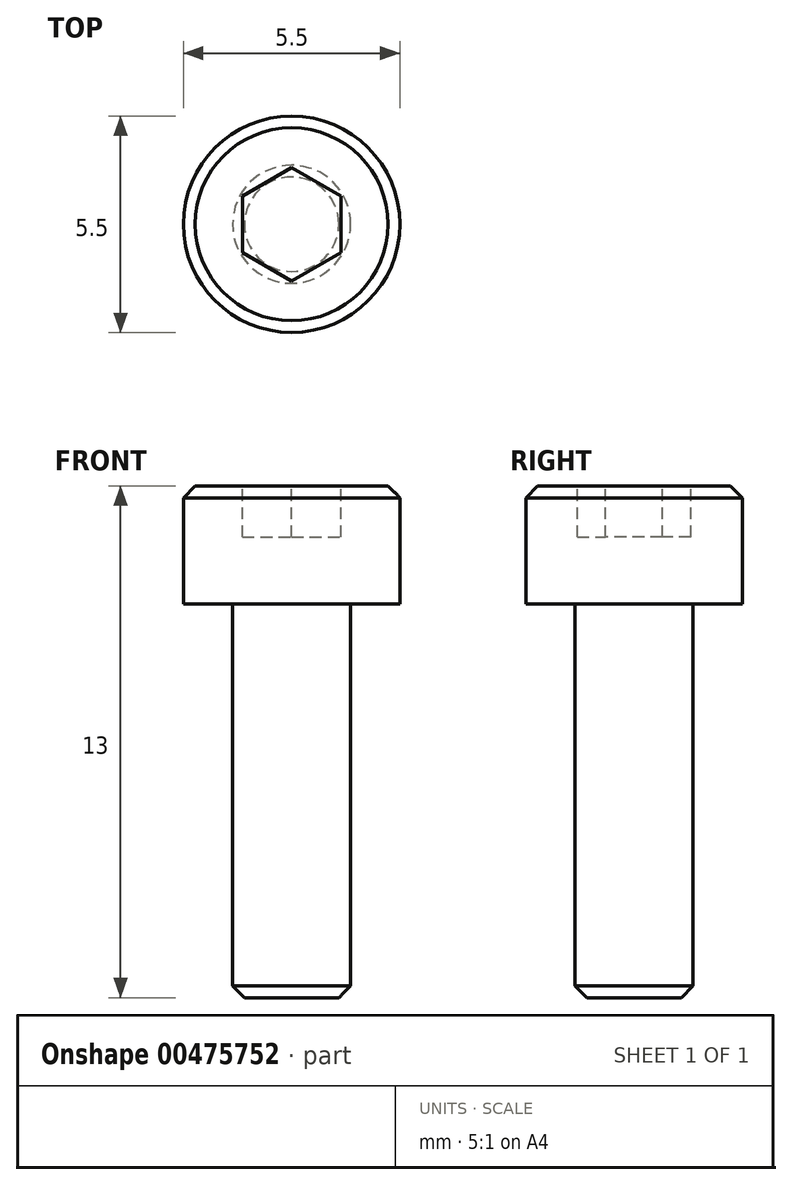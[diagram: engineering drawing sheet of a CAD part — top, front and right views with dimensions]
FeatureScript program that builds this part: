
annotation { "Feature Type Name" : "Feature", "Feature Type Description" : "" }
export const myFeature = defineFeature(function(context is Context, id is Id, definition is map)
    precondition{}
    {
        {
            assignVariable(context, id + "F0", {"name" : "M", "anyValue" : 3});
        }
        {
            assignVariable(context, id + "F1", {"name" : "length", "anyValue" : 10});
        }
        {
            var Q0;
            Q0=qCreatedBy(makeId("Top.planeOp"),FACE);
            var sketch = newSketch(context, id + "F2", { "sketchPlane" : qUnion([Q0])});
            skCircle(sketch, "E0", {"center": v(0, 0) * mm, "radius": 1.5 * mm});
            skCircle(sketch, "E1", {"center": v(0, 0) * mm, "radius": 2.75 * mm});
            skSolve(sketch);
        }
        {
            var Q0;
            Q0=makeQuery(id+"F2.imprint","IMPRINT",FACE,{"disambiguationData":[TD([[makeQuery(id+"F2.imprint","IMPRINT",EDGE,{"derivedFrom":sQuery(id+"F2.wireOp",EDGE,"E0")}),1.0]])]});
            extrude(context, id + "F3", {"entities" : qUnion([Q0]), "oppositeDirection" : true, "depth" : getVariable(context, 'length') * mm});
        }
        {
            var Q0;
            Q0=qSketchRegion(id+"F2",true);
            var Q1;
            Q1=makeQuery(id+"F3.opExtrude","CAP_FACE",FACE,{"disambiguationData":[OSD([sQuery(id+"F2.wireOp",EDGE,"E0")])],"isStart":true});
            extrude(context, id + "F4", {"entities" : qUnion([Q0, Q1]), "operationType" : NewBodyOperationType.ADD, "depth" : (getVariable(context, 'M')) * mm});
        }
        {
            var Q0;
            Q0=makeQuery(id+"F3.opExtrude","CAP_EDGE",EDGE,{"disambiguationData":[OSD([sQuery(id+"F2.wireOp",EDGE,"E0")])],"isStart":false});
            var Q1;
            Q1=makeQuery(id+"F4.opExtrude","CAP_EDGE",EDGE,{"disambiguationData":[OSD([sQuery(id+"F2.wireOp",EDGE,"E1")])],"isStart":false});
            var Q2;
            Q2=makeQuery(id+"FbGFCUzPbhfoxTw_1.opExtrude","CAP_EDGE",EDGE,{"disambiguationData":[OSD([sQuery(id+"FgaPx5IOfmBmuk3_1.wireOp",EDGE,"RfBxyrST-LDbJ-RpBC-vAS8-07GQ8Ko211GC")])],"isStart":false});
            chamfer(context, id + "F5", {"entities" : qUnion([Q0, Q1, Q2]), "width" : 0.3 * mm, "tangentPropagation" : true});
        }
        {
            var Q0;
            {var subQ0=sQuery(id+"F2.wireOp",EDGE,"E0");Q0=makeQuery(id+"F4.boolean.opBoolean","MERGE",FACE,{"derivedFrom":[makeQuery(id+"F4.opExtrude","CAP_FACE",FACE,{"disambiguationData":[OSD([subQ0,sQuery(id+"F2.wireOp",EDGE,"E1")])],"isStart":false}),makeQuery(id+"F4.opExtrude","CAP_FACE",FACE,{"disambiguationData":[OSD([subQ0])],"isStart":false})]});}
            var sketch = newSketch(context, id + "F6", { "sketchPlane" : qUnion([Q0])});
            skCircle(sketch, "E2.cCircle", {"center": v(0, 0) * mm, "radius": 1.25 * mm, "construction": true});
            skLineSegment(sketch, "E2.0", {"start": v(1.25, 0.72) * mm, "end": v(1.25, -0.72) * mm});
            skLineSegment(sketch, "E2.1", {"start": v(1.25, -0.72) * mm, "end": v(0, -1.44) * mm});
            skLineSegment(sketch, "E2.2", {"start": v(0, -1.44) * mm, "end": v(-1.25, -0.72) * mm});
            skLineSegment(sketch, "E2.3", {"start": v(-1.25, -0.72) * mm, "end": v(-1.25, 0.72) * mm});
            skLineSegment(sketch, "E2.4", {"start": v(-1.25, 0.72) * mm, "end": v(0, 1.44) * mm});
            skLineSegment(sketch, "E2.5", {"start": v(0, 1.44) * mm, "end": v(1.25, 0.72) * mm});
            skPoint(sketch, "E2.0.midPoint", {"position": v(1.25, 0) * mm});
            skSolve(sketch);
        }
        {
            var Q0;
            Q0=makeQuery(id+"F6.imprint","IMPRINT",FACE,{"disambiguationData":[TD([[makeQuery(id+"F6.imprint","IMPRINT",EDGE,{"derivedFrom":sQuery(id+"F6.wireOp",EDGE,"E2.0")}),-1.0]])]});
            extrude(context, id + "F7", {"entities" : qUnion([Q0]), "operationType" : NewBodyOperationType.REMOVE, "oppositeDirection" : true, "depth" : 1.3 * mm, "offsetDistance" : 25 * mm});
        }
    });
